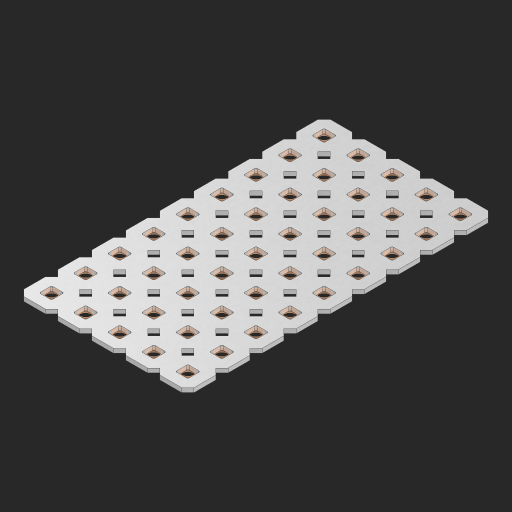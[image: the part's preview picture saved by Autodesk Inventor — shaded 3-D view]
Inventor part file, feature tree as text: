
AUTODESK INVENTOR PART (.ipt)
format: ipt  version: 2023 (Build 270158000, 158)  size: 814,592 bytes
history: native  units: in
note: dims shown in document units (in); Inventor stores cm internally (conversion verified against a paired STEP export)
features: other x46, extrude x44, sketch x2, pattern_linear x1
ambient origin geometry x8: Origin, YZ Plane, XZ Plane, XY Plane, X Axis, Y Axis, Z Axis, Center Point
bodies: Solid1 (feature_tree), Body (feature_tree)
feature tree (93):
  pattern_linear  "Rectangular Pattern1"  Spacing1=0.09in  [1 undecoded]
  sketch  "Sketch1"  dims[d1=0.5in]
  sketch  "Sketch2"  dims[d2=0.182in d3=0.09in d4=0.09in d5=0.09in d6=0.09in d7=0.09in d8=0.09in d9=0.09in d10=0.09in d11=0.02in d13=0.0in d14=0.172in d15=0.0625in d16=0.0in d19=0.5in d22=0.5in]
  other  "Srf1"
  other  "Srf126"
  other  "Srf127"
  other  "Srf128"
  other  "Srf129"
  other  "Srf130"
  other  "Srf131"
  other  "Srf250"
  other  "Srf268"
  other  "Srf269"
  other  "Srf270"
  other  "Srf271"
  other  "Srf272"
  other  "Srf273"
  other  "Srf274"
  other  "Srf275"
  other  "Srf293"
  other  "Srf294"
  other  "Srf295"
  other  "Srf296"
  other  "Srf297"
  other  "Srf298"
  other  "Srf299"
  other  "Srf300"
  other  "Srf318"
  other  "Srf319"
  other  "Srf320"
  other  "Srf321"
  other  "Srf322"
  other  "Srf323"
  other  "Srf324"
  other  "Srf325"
  other  "Srf343"
  other  "Srf344"
  other  "Srf345"
  other  "Srf346"
  other  "Srf347"
  other  "Srf348"
  other  "Srf349"
  other  "Srf350"
  other  "Srf368"
  other  "Srf369"
  other  "Srf370"
  other  "Srf371"
  other  "Srf372"
  other  "Circle"
  extrude  "ExtrusionSrf126"  Depth=0.09in
  extrude  "ExtrusionSrf127"  Depth=0.09in
  extrude  "ExtrusionSrf128"  Depth=0.09in
  extrude  "ExtrusionSrf129"  Depth=0.09in
  extrude  "ExtrusionSrf130"  Depth=0.09in
  extrude  "ExtrusionSrf131"  Depth=0.09in
  extrude  "ExtrusionSrf250"  Depth=0.09in
  extrude  "ExtrusionSrf268"  Depth=0.02in
  extrude  "ExtrusionSrf269"  TaperAngle=0.0deg  [1 undecoded]
  extrude  "ExtrusionSrf270"  Depth=0.5in
  extrude  "ExtrusionSrf271"  Depth=0.0625in TaperAngle=0.0deg
  extrude  "ExtrusionSrf272"  Depth=0.5in
  extrude  "ExtrusionSrf273"  Depth=0.5in
  extrude  "ExtrusionSrf274"  [1 undecoded]
  extrude  "ExtrusionSrf275"  [1 undecoded]
  extrude  "ExtrusionSrf293"  [1 undecoded]
  extrude  "ExtrusionSrf294"  [1 undecoded]
  extrude  "ExtrusionSrf295"  [1 undecoded]
  extrude  "ExtrusionSrf296"  [1 undecoded]
  extrude  "ExtrusionSrf297"  [1 undecoded]
  extrude  "ExtrusionSrf298"  [1 undecoded]
  extrude  "ExtrusionSrf299"  [1 undecoded]
  extrude  "ExtrusionSrf300"  [1 undecoded]
  extrude  "ExtrusionSrf318"  [1 undecoded]
  extrude  "ExtrusionSrf319"  [1 undecoded]
  extrude  "ExtrusionSrf320"  [1 undecoded]
  extrude  "ExtrusionSrf321"  [1 undecoded]
  extrude  "ExtrusionSrf322"  [1 undecoded]
  extrude  "ExtrusionSrf323"  [1 undecoded]
  extrude  "ExtrusionSrf324"  [1 undecoded]
  extrude  "ExtrusionSrf325"  [1 undecoded]
  extrude  "ExtrusionSrf343"  [1 undecoded]
  extrude  "ExtrusionSrf344"  [1 undecoded]
  extrude  "ExtrusionSrf345"  [1 undecoded]
  extrude  "ExtrusionSrf346"  [1 undecoded]
  extrude  "ExtrusionSrf347"  [1 undecoded]
  extrude  "ExtrusionSrf348"  [1 undecoded]
  extrude  "ExtrusionSrf349"  [1 undecoded]
  extrude  "ExtrusionSrf350"  [1 undecoded]
  extrude  "ExtrusionSrf368"  [1 undecoded]
  extrude  "ExtrusionSrf369"  [1 undecoded]
  extrude  "ExtrusionSrf370"  [1 undecoded]
  extrude  "ExtrusionSrf371"  [1 undecoded]
  extrude  "ExtrusionSrf372"  [1 undecoded]
note: 33 required parameter values undecoded (feature->parameter linkage not recoverable at this tier; creation-order binding heuristic only, values carry confidence <= 0.55)
